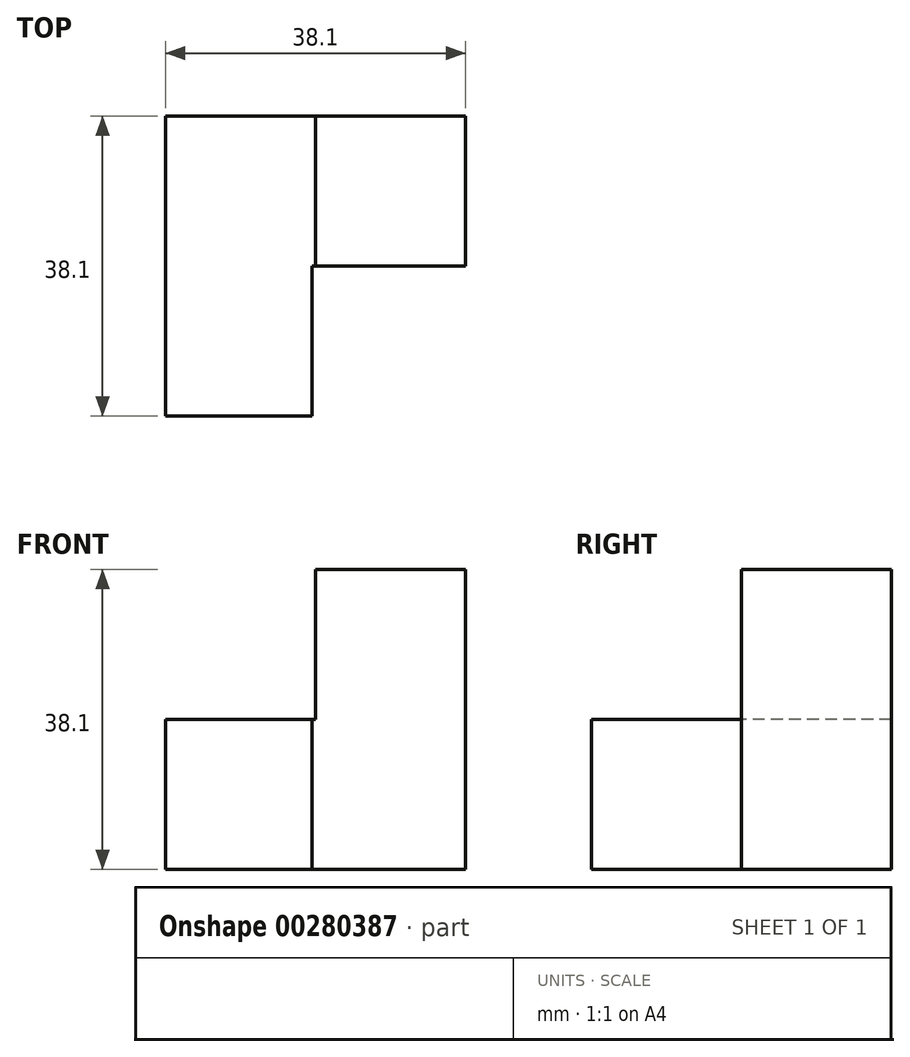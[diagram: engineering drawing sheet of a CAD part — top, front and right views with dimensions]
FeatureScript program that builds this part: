
annotation { "Feature Type Name" : "Feature", "Feature Type Description" : "" }
export const myFeature = defineFeature(function(context is Context, id is Id, definition is map)
    precondition{}
    {
        {
            var Q0;
            Q0=qCreatedBy(makeId("Top.planeOp"),FACE);
            var sketch = newSketch(context, id + "F0", { "sketchPlane" : qUnion([Q0])});
            skLineSegment(sketch, "E0.bottom", {"start": v(0, 0) * mm, "end": v(18.6, 0) * mm});
            skLineSegment(sketch, "E0.top", {"start": v(0, 38.1) * mm, "end": v(38.1, 38.1) * mm});
            skLineSegment(sketch, "E0.left", {"start": v(0, 0) * mm, "end": v(0, 38.1) * mm});
            skLineSegment(sketch, "E0.right", {"start": v(38.1, 19.05) * mm, "end": v(38.1, 38.1) * mm});
            skLineSegment(sketch, "E1", {"start": v(38.1, 19.05) * mm, "end": v(18.6, 19.05) * mm});
            skLineSegment(sketch, "E2", {"start": v(18.6, 0) * mm, "end": v(18.6, 19.05) * mm});
            skPoint(sketch, "E3.orphan", {"position": v(38.1, 0) * mm});
            skSolve(sketch);
        }
        {
            var Q0;
            Q0=makeQuery(id+"F0.imprint","IMPRINT",FACE,{"disambiguationData":[TD([[makeQuery(id+"F0.imprint","IMPRINT",EDGE,{"derivedFrom":sQuery(id+"F0.wireOp",EDGE,"E0.bottom")}),1.0]])]});
            extrude(context, id + "F1", {"entities" : qUnion([Q0]), "depth" : 19.05 * mm});
        }
        {
            var Q0;
            Q0=makeQuery(id+"F1.opExtrude","CAP_FACE",FACE,{"disambiguationData":[OSD([sQuery(id+"F0.wireOp",EDGE,"E0.bottom"),sQuery(id+"F0.wireOp",EDGE,"E0.top"),sQuery(id+"F0.wireOp",EDGE,"E0.left"),sQuery(id+"F0.wireOp",EDGE,"E0.right"),sQuery(id+"F0.wireOp",EDGE,"E1"),sQuery(id+"F0.wireOp",EDGE,"E2")])],"isStart":false});
            var sketch = newSketch(context, id + "F2", { "sketchPlane" : qUnion([Q0])});
            skLineSegment(sketch, "E4.bottom", {"start": v(19.05, 38.1) * mm, "end": v(38.1, 38.1) * mm});
            skLineSegment(sketch, "E4.top", {"start": v(19.05, 19.05) * mm, "end": v(38.1, 19.05) * mm});
            skLineSegment(sketch, "E4.left", {"start": v(19.05, 38.1) * mm, "end": v(19.05, 19.05) * mm});
            skLineSegment(sketch, "E4.right", {"start": v(38.1, 38.1) * mm, "end": v(38.1, 19.05) * mm});
            skSolve(sketch);
        }
        {
            var Q0;
            Q0=makeQuery(id+"F2.imprint","IMPRINT",FACE,{"disambiguationData":[TD([[makeQuery(id+"F2.imprint","IMPRINT",EDGE,{"derivedFrom":sQuery(id+"F2.wireOp",EDGE,"E4.bottom")}),-1.0]])]});
            extrude(context, id + "F3", {"entities" : qUnion([Q0]), "operationType" : NewBodyOperationType.ADD, "depth" : 19.05 * mm});
        }
    });
